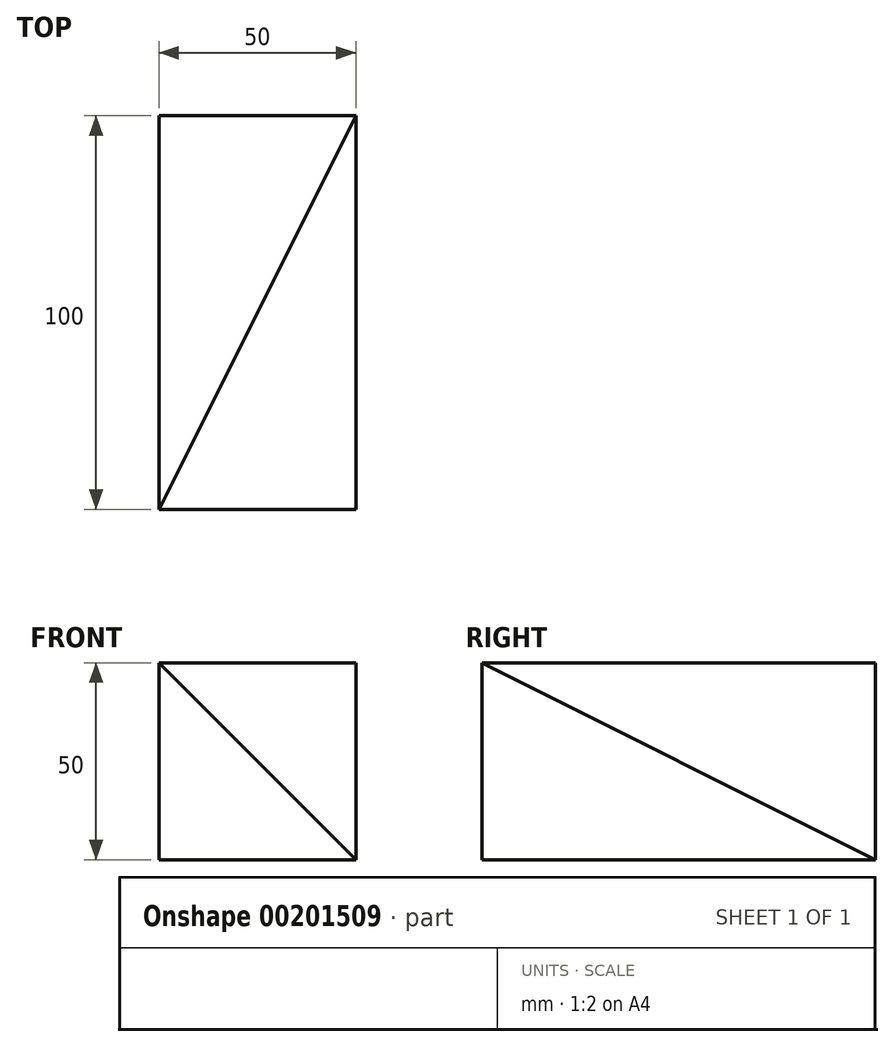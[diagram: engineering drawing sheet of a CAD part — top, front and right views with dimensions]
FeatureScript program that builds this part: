
annotation { "Feature Type Name" : "Feature", "Feature Type Description" : "" }
export const myFeature = defineFeature(function(context is Context, id is Id, definition is map)
    precondition{}
    {
        {
            var Q0;
            Q0=qCreatedBy(makeId("Top.planeOp"),FACE);
            var sketch = newSketch(context, id + "F0", { "sketchPlane" : qUnion([Q0])});
            skLineSegment(sketch, "E0", {"start": v(0, 0) * mm, "end": v(0, 100) * mm});
            skLineSegment(sketch, "E1", {"start": v(0, 100) * mm, "end": v(50, 100) * mm});
            skLineSegment(sketch, "E2", {"start": v(50, 100) * mm, "end": v(0, 0) * mm});
            skSolve(sketch);
        }
        {
            var Q0;
            Q0=qSketchRegion(id+"F0",true);
            extrude(context, id + "F1", {"entities" : qUnion([Q0]), "depth" : 50 * mm});
        }
        {
            var Q0;
            Q0=qCreatedBy(makeId("Front.planeOp"),FACE);
            var sketch = newSketch(context, id + "F2", { "sketchPlane" : qUnion([Q0])});
            skLineSegment(sketch, "E3.0", {"start": v(0, 50) * mm, "end": v(0, 0) * mm});
            skLineSegment(sketch, "E4", {"start": v(0, 50) * mm, "end": v(50, 0) * mm});
            skLineSegment(sketch, "E5", {"start": v(50, 0) * mm, "end": v(0, 0) * mm});
            skSolve(sketch);
        }
        {
            var Q0;
            Q0=qSketchRegion(id+"F2",true);
            var Q1;
            Q1=makeQuery(id+"F1.opExtrude","CAP_VERTEX",VERTEX,{"disambiguationData":[OSD([sQuery(id+"F0.wireOp",EDGE,"E1"),sQuery(id+"F0.wireOp",EDGE,"E2")])],"isStart":true});
            extrude(context, id + "F3", {"entities" : qUnion([Q0]), "operationType" : NewBodyOperationType.ADD, "endBound" : BoundingType.UP_TO_VERTEX, "oppositeDirection" : true, "endBoundEntityVertex" : qUnion([Q1]), "depth" : 25 * mm});
        }
    });
